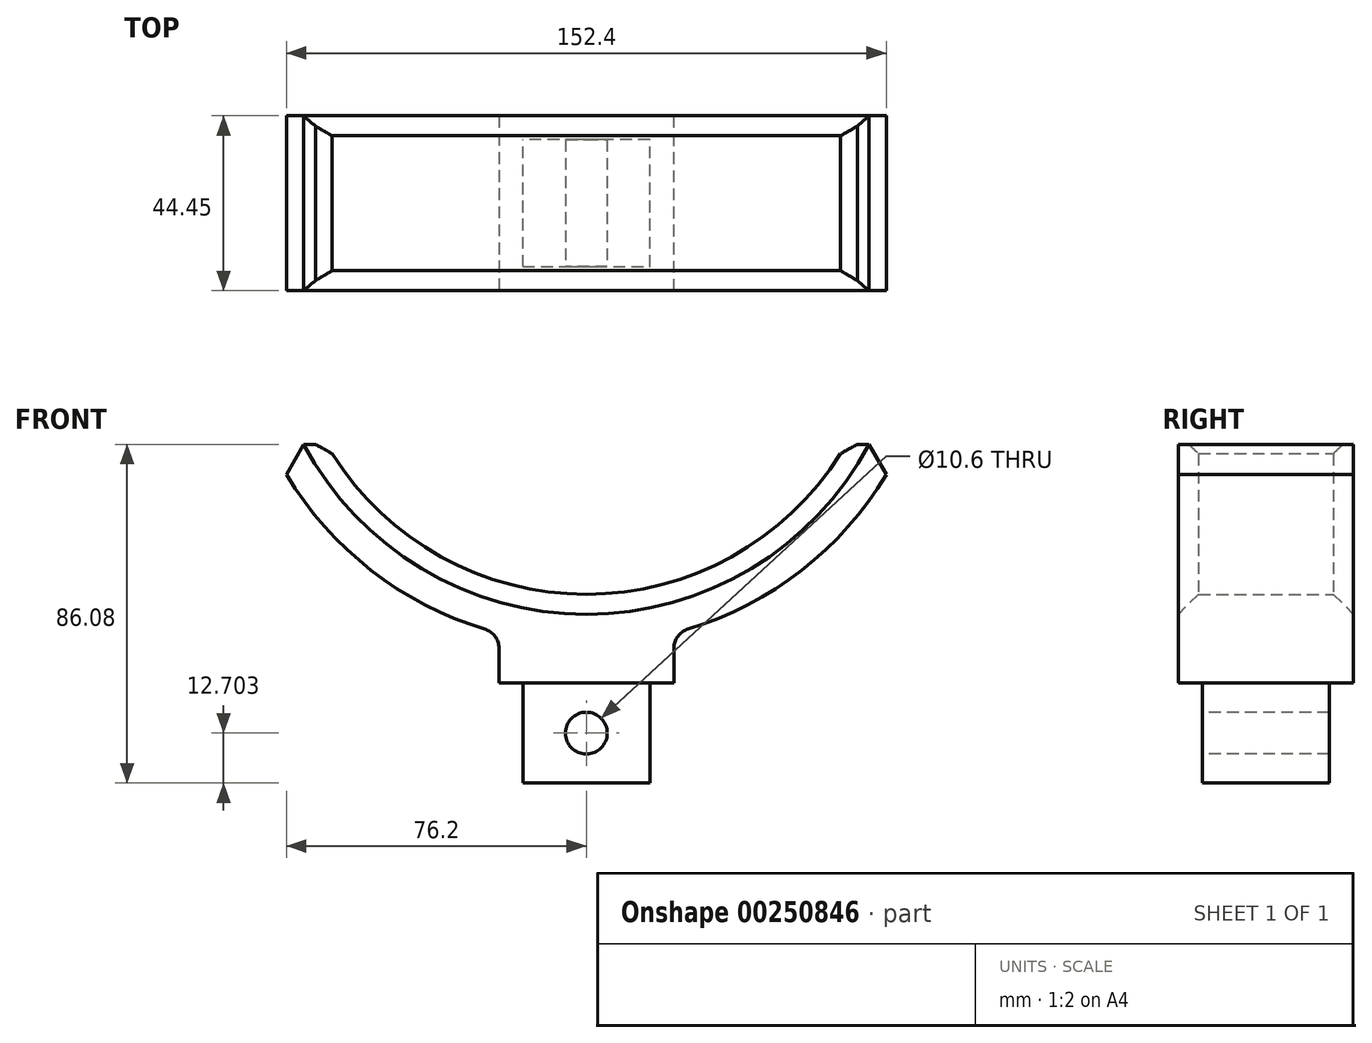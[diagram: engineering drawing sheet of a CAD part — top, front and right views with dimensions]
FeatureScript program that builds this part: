
annotation { "Feature Type Name" : "Feature", "Feature Type Description" : "" }
export const myFeature = defineFeature(function(context is Context, id is Id, definition is map)
    precondition{}
    {
        {
            var Q0;
            Q0=qCreatedBy(makeId("Front.planeOp"),FACE);
            var sketch = newSketch(context, id + "F0", { "sketchPlane" : qUnion([Q0])});
            skCircle(sketch, "E0", {"center": v(0, 0) * mm, "radius": 76.2 * mm});
            skCircle(sketch, "E1", {"center": v(0, 0) * mm, "radius": 88.9 * mm});
            skLineSegment(sketch, "E2", {"start": v(0, 0) * mm, "end": v(0, -88.9) * mm});
            skLineSegment(sketch, "E3", {"start": v(-66, -38.1) * mm, "end": v(66, -38.1) * mm});
            skLineSegment(sketch, "E4", {"start": v(-66, -38.1) * mm, "end": v(-80.32, -38.1) * mm});
            skLineSegment(sketch, "E5", {"start": v(66, -38.1) * mm, "end": v(80.32, -38.1) * mm});
            skLineSegment(sketch, "E6.bottom", {"start": v(-22.22, -86.08) * mm, "end": v(22.22, -86.08) * mm});
            skLineSegment(sketch, "E6.top", {"start": v(-22.22, -98.78) * mm, "end": v(22.22, -98.78) * mm});
            skLineSegment(sketch, "E6.left", {"start": v(-22.22, -86.08) * mm, "end": v(-22.22, -98.78) * mm});
            skLineSegment(sketch, "E6.right", {"start": v(22.22, -86.08) * mm, "end": v(22.22, -98.78) * mm});
            skLineSegment(sketch, "E7.bottom", {"start": v(-16.13, -98.78) * mm, "end": v(16.13, -98.78) * mm});
            skLineSegment(sketch, "E7.top", {"start": v(-16.13, -124.18) * mm, "end": v(16.13, -124.18) * mm});
            skLineSegment(sketch, "E7.left", {"start": v(-16.13, -98.78) * mm, "end": v(-16.13, -124.18) * mm});
            skLineSegment(sketch, "E7.right", {"start": v(16.13, -98.78) * mm, "end": v(16.13, -124.18) * mm});
            skLineSegment(sketch, "E8", {"start": v(0, -88.9) * mm, "end": v(0, -124.18) * mm});
            skSolve(sketch);
        }
        {
            var Q0;
            {var subQ0=sQuery(id+"F0.wireOp",EDGE,"E4");Q0=makeQuery(id+"F0.imprint","IMPRINT",FACE,{"disambiguationData":[TD([[makeQuery(id+"F0.imprint","IMPRINT",EDGE,{"derivedFrom":subQ0}),1.0]])]});}
            var Q1;
            {var subQ0=sQuery(id+"F0.wireOp",EDGE,"E5");Q1=makeQuery(id+"F0.imprint","IMPRINT",FACE,{"disambiguationData":[TD([[makeQuery(id+"F0.imprint","IMPRINT",EDGE,{"derivedFrom":subQ0}),-1.0]])]});}
            var Q2;
            {var subQ0=sQuery(id+"F0.wireOp",EDGE,"E6.right");Q2=makeQuery(id+"F0.imprint","IMPRINT",FACE,{"disambiguationData":[TD([[makeQuery(id+"F0.imprint","IMPRINT",EDGE,{"derivedFrom":subQ0}),-1.0]])]});}
            var Q3;
            {var subQ0=sQuery(id+"F0.wireOp",EDGE,"E6.left");Q3=makeQuery(id+"F0.imprint","IMPRINT",FACE,{"disambiguationData":[TD([[makeQuery(id+"F0.imprint","IMPRINT",EDGE,{"derivedFrom":subQ0}),1.0]])]});}
            var Q4;
            {var subQ0=sQuery(id+"F0.wireOp",EDGE,"E7.right");Q4=makeQuery(id+"F0.imprint","IMPRINT",FACE,{"disambiguationData":[TD([[makeQuery(id+"F0.imprint","IMPRINT",EDGE,{"derivedFrom":subQ0}),-1.0]])]});}
            var Q5;
            {var subQ0=sQuery(id+"F0.wireOp",EDGE,"E7.left");Q5=makeQuery(id+"F0.imprint","IMPRINT",FACE,{"disambiguationData":[TD([[makeQuery(id+"F0.imprint","IMPRINT",EDGE,{"derivedFrom":subQ0}),1.0]])]});}
            var Q6;
            {var subQ0=sQuery(id+"F0.wireOp",EDGE,"E2");var subQ3=sQuery(id+"F0.wireOp",EDGE,"E6.bottom");var subQ5=makeQuery(id+"F0.imprint","INTERSECT",VERTEX,{"derivedFrom":[subQ0,subQ3]});Q6=makeQuery(id+"F0.imprint","IMPRINT",FACE,{"disambiguationData":[TD([[makeQuery(id+"F0.imprint","IMPRINT",EDGE,{"disambiguationData":[TD([[subQ5,-1.0]])],"derivedFrom":subQ0}),1.0]])]});}
            var Q7;
            {var subQ0=sQuery(id+"F0.wireOp",EDGE,"E2");var subQ3=sQuery(id+"F0.wireOp",EDGE,"E6.bottom");var subQ5=makeQuery(id+"F0.imprint","INTERSECT",VERTEX,{"derivedFrom":[subQ0,subQ3]});Q7=makeQuery(id+"F0.imprint","IMPRINT",FACE,{"disambiguationData":[TD([[makeQuery(id+"F0.imprint","IMPRINT",EDGE,{"disambiguationData":[TD([[subQ5,-1.0]])],"derivedFrom":subQ0}),-1.0]])]});}
            extrude(context, id + "F1", {"entities" : qUnion([Q0, Q1, Q2, Q3, Q4, Q5, Q6, Q7]), "depth" : 44.45 * mm});
        }
        {
            var Q0;
            Q0=makeQuery(id+"F1.opExtrude","SWEPT_FACE",FACE,{"disambiguationData":[OSD([sQuery(id+"F0.wireOp",EDGE,"E7.top")])]});
            var sketch = newSketch(context, id + "F2", { "sketchPlane" : qUnion([Q0])});
            skLineSegment(sketch, "E9.bottom", {"start": v(-16.13, 44.45) * mm, "end": v(16.13, 44.45) * mm});
            skLineSegment(sketch, "E9.top", {"start": v(-16.13, 38.35) * mm, "end": v(16.13, 38.35) * mm});
            skLineSegment(sketch, "E9.left", {"start": v(-16.13, 44.45) * mm, "end": v(-16.13, 38.35) * mm});
            skLineSegment(sketch, "E9.right", {"start": v(16.13, 44.45) * mm, "end": v(16.13, 38.35) * mm});
            skLineSegment(sketch, "E10.bottom", {"start": v(16.13, 0) * mm, "end": v(-16.13, 0) * mm});
            skLineSegment(sketch, "E10.top", {"start": v(16.13, 6.1) * mm, "end": v(-16.13, 6.1) * mm});
            skLineSegment(sketch, "E10.left", {"start": v(16.13, 0) * mm, "end": v(16.13, 6.1) * mm});
            skLineSegment(sketch, "E10.right", {"start": v(-16.13, 0) * mm, "end": v(-16.13, 6.1) * mm});
            skSolve(sketch);
        }
        {
            var Q0;
            Q0 = qSketchRegion(id + "F2", true);
            extrude(context, id + "F3", {"entities" : qUnion([Q0]), "operationType" : NewBodyOperationType.REMOVE, "oppositeDirection" : true, "depth" : 25.4 * mm});
        }
        {
            var Q0;
            Q0=makeQuery(id+"F3.boolean.opBoolean","COPY",FACE,{"derivedFrom":makeQuery(id+"F3.opExtrude","SWEPT_FACE",FACE,{"disambiguationData":[OSD([sQuery(id+"F2.wireOp",EDGE,"E9.top")])]})});
            var sketch = newSketch(context, id + "F4", { "sketchPlane" : qUnion([Q0])});
            skCircle(sketch, "E11", {"center": v(0, -111.48) * mm, "radius": 5.3 * mm});
            skSolve(sketch);
        }
        {
            var Q0;
            Q0 = qSketchRegion(id + "F4", true);
            extrude(context, id + "F5", {"entities" : qUnion([Q0]), "operationType" : NewBodyOperationType.REMOVE, "endBound" : BoundingType.THROUGH_ALL, "oppositeDirection" : true, "depth" : 25.4 * mm});
        }
        {
            var Q0;
            Q0=makeQuery(id+"F1.opExtrude","SWEPT_EDGE",EDGE,{"disambiguationData":[OSD([sQuery(id+"F0.wireOp",EDGE,"E1"),sQuery(id+"F0.wireOp",EDGE,"E6.bottom"),sQuery(id+"F0.wireOp",EDGE,"E6.left")])]});
            var Q1;
            Q1=makeQuery(id+"F1.opExtrude","SWEPT_EDGE",EDGE,{"disambiguationData":[OSD([sQuery(id+"F0.wireOp",EDGE,"E1"),sQuery(id+"F0.wireOp",EDGE,"E6.bottom"),sQuery(id+"F0.wireOp",EDGE,"E6.right")])]});
            fillet(context, id + "F6", {"entities" : qUnion([Q0, Q1]), "radius" : 5.08 * mm, "tangentPropagation" : true, "allowEdgeOverflow" : false});
        }
        {
            var Q0;
            Q0=makeQuery(id+"F1.opExtrude","CAP_EDGE",EDGE,{"disambiguationData":[OSD([sQuery(id+"F0.wireOp",EDGE,"E0")])],"isStart":false});
            var Q1;
            Q1=makeQuery(id+"F1.opExtrude","CAP_EDGE",EDGE,{"disambiguationData":[OSD([sQuery(id+"F0.wireOp",EDGE,"E0")])],"isStart":true});
            var Q2;
            Q2=makeQuery(id+"F1.opExtrude","SWEPT_EDGE",EDGE,{"disambiguationData":[OSD([sQuery(id+"F0.wireOp",EDGE,"E0"),sQuery(id+"F0.wireOp",EDGE,"E3"),sQuery(id+"F0.wireOp",EDGE,"E4")])]});
            var Q3;
            Q3=makeQuery(id+"F1.opExtrude","SWEPT_EDGE",EDGE,{"disambiguationData":[OSD([sQuery(id+"F0.wireOp",EDGE,"E0"),sQuery(id+"F0.wireOp",EDGE,"E3"),sQuery(id+"F0.wireOp",EDGE,"E5")])]});
            chamfer(context, id + "F7", {"entities" : qUnion([Q0, Q1, Q2, Q3]), "width" : 5.08 * mm, "tangentPropagation" : true});
        }
        {
            var Q0;
            Q0=makeQuery(id+"F1.opExtrude","SWEPT_EDGE",EDGE,{"disambiguationData":[OSD([sQuery(id+"F0.wireOp",EDGE,"E1"),sQuery(id+"F0.wireOp",EDGE,"E5")])]});
            var Q1;
            Q1=makeQuery(id+"F1.opExtrude","SWEPT_EDGE",EDGE,{"disambiguationData":[OSD([sQuery(id+"F0.wireOp",EDGE,"E1"),sQuery(id+"F0.wireOp",EDGE,"E4")])]});
            chamfer(context, id + "F8", {"entities" : qUnion([Q0, Q1]), "width" : 5.08 * mm, "tangentPropagation" : true});
        }
    });
